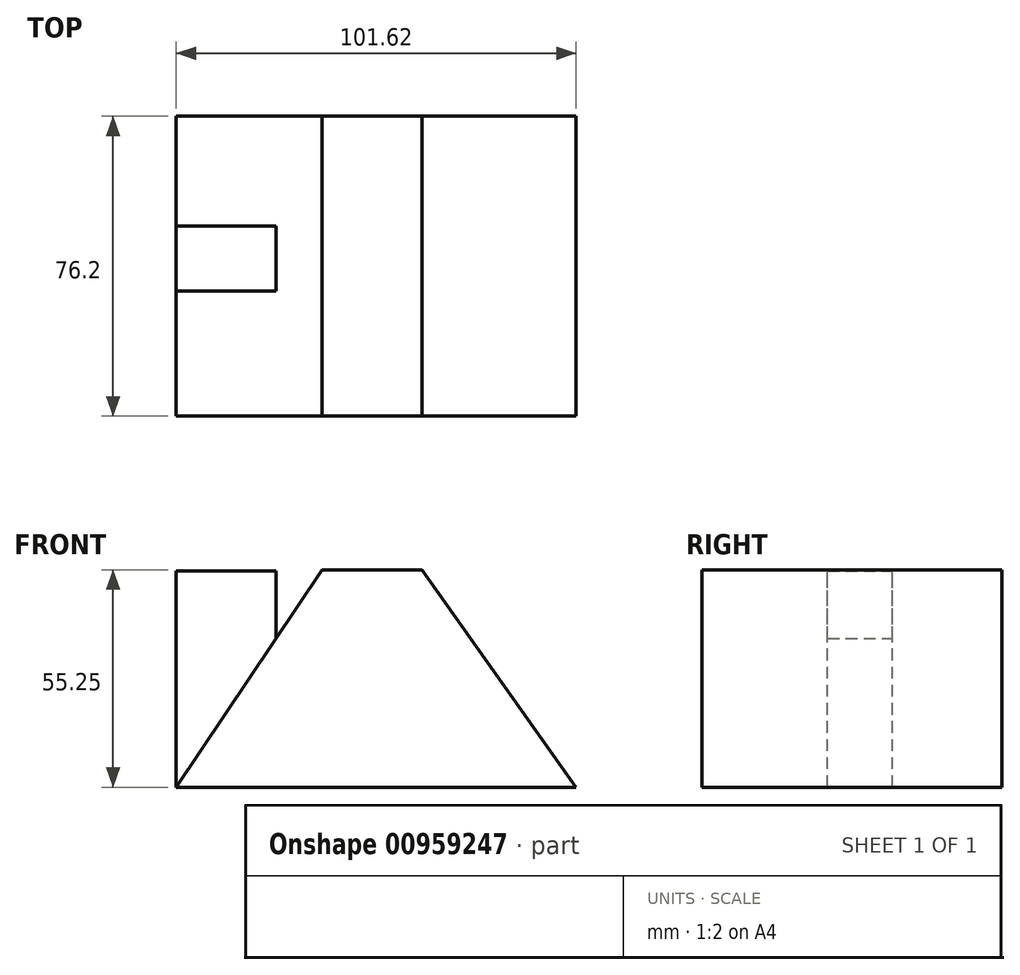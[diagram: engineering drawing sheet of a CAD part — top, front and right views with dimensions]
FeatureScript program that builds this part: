
annotation { "Feature Type Name" : "Feature", "Feature Type Description" : "" }
export const myFeature = defineFeature(function(context is Context, id is Id, definition is map)
    precondition{}
    {
        {
            var Q0;
            Q0=qCreatedBy(makeId("Front.planeOp"),FACE);
            var sketch = newSketch(context, id + "F0", { "sketchPlane" : qUnion([Q0])});
            skLineSegment(sketch, "E0", {"start": v(37.1, 55.25) * mm, "end": v(76.22, 0) * mm});
            skLineSegment(sketch, "E1", {"start": v(76.22, 0) * mm, "end": v(0, 0) * mm});
            skLineSegment(sketch, "E2", {"start": v(0, 0) * mm, "end": v(37.1, 55.25) * mm});
            skSolve(sketch);
        }
        {
            var Q0;
            Q0=makeQuery(id+"F0.imprint","IMPRINT",FACE,{"disambiguationData":[TD([[makeQuery(id+"F0.imprint","IMPRINT",EDGE,{"derivedFrom":sQuery(id+"F0.wireOp",EDGE,"E0")}),-1.0]])]});
            extrude(context, id + "F1", {"entities" : qUnion([Q0]), "depth" : 76.2 * mm, "offsetDistance" : 25.4 * mm});
        }
        {
            var Q0;
            Q0=qCreatedBy(makeId("Right.planeOp"),FACE);
            var sketch = newSketch(context, id + "F2", { "sketchPlane" : qUnion([Q0])});
            skLineSegment(sketch, "E3.bottom", {"start": v(-44.35, 0) * mm, "end": v(-27.83, 0) * mm});
            skLineSegment(sketch, "E3.top", {"start": v(-44.35, 54.95) * mm, "end": v(-27.83, 54.95) * mm});
            skLineSegment(sketch, "E3.left", {"start": v(-44.35, 0) * mm, "end": v(-44.35, 54.95) * mm});
            skLineSegment(sketch, "E3.right", {"start": v(-27.83, 0) * mm, "end": v(-27.83, 54.95) * mm});
            skSolve(sketch);
        }
        {
            var Q0;
            Q0 = qSketchRegion(id + "F2", true);
            var Q1;
            Q1=makeQuery(id+"F1.opExtrude","SWEPT_FACE",FACE,{"disambiguationData":[OSD([sQuery(id+"F0.wireOp",EDGE,"E0")])]});
            extrude(context, id + "F3", {"entities" : qUnion([Q0, Q1]), "operationType" : NewBodyOperationType.ADD, "depth" : 25.4 * mm, "offsetDistance" : 25.4 * mm});
        }
    });
